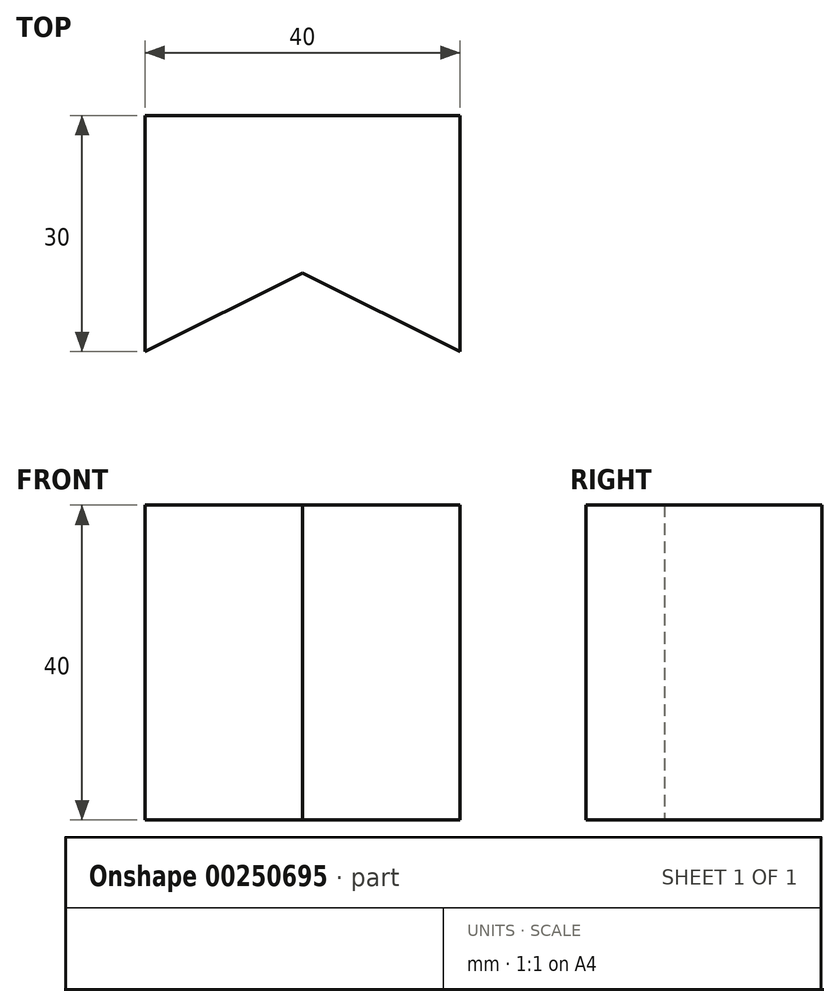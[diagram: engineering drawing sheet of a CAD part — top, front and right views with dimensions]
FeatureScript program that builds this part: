
annotation { "Feature Type Name" : "Feature", "Feature Type Description" : "" }
export const myFeature = defineFeature(function(context is Context, id is Id, definition is map)
    precondition{}
    {
        {
            var Q0;
            Q0=qCreatedBy(makeId("Top.planeOp"),FACE);
            var sketch = newSketch(context, id + "F0", { "sketchPlane" : qUnion([Q0])});
            skLineSegment(sketch, "E0.top", {"start": v(0, 30) * mm, "end": v(40, 30) * mm});
            skLineSegment(sketch, "E0.left", {"start": v(0, 0) * mm, "end": v(0, 30) * mm});
            skLineSegment(sketch, "E0.right", {"start": v(40, 0) * mm, "end": v(40, 30) * mm});
            skLineSegment(sketch, "E1", {"start": v(20, 30) * mm, "end": v(20, 10) * mm});
            skLineSegment(sketch, "E2", {"start": v(20, 10) * mm, "end": v(40, 0) * mm});
            skLineSegment(sketch, "E3", {"start": v(20, 10) * mm, "end": v(0, 0) * mm});
            skSolve(sketch);
        }
        {
            var Q0;
            Q0 = qSketchRegion(id + "F0", true);
            extrude(context, id + "F1", {"entities" : qUnion([Q0]), "depth" : 40 * mm});
        }
    });
